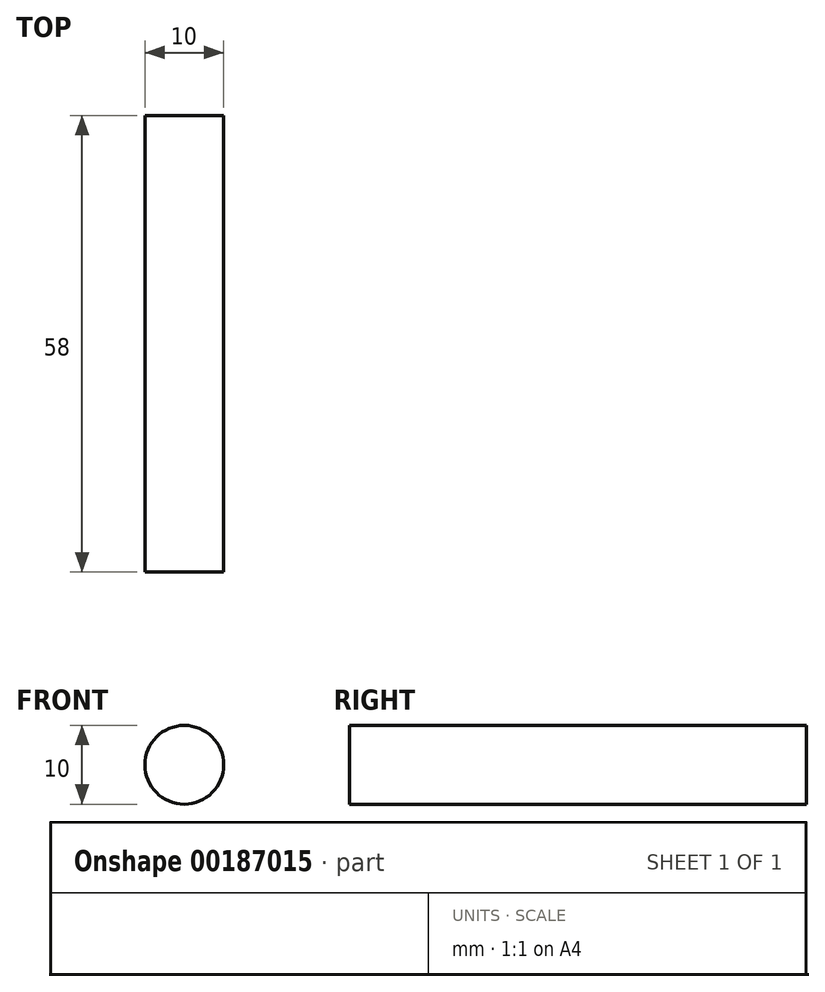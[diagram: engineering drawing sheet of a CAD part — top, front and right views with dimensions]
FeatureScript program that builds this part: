
annotation { "Feature Type Name" : "Feature", "Feature Type Description" : "" }
export const myFeature = defineFeature(function(context is Context, id is Id, definition is map)
    precondition{}
    {
        {
            var Q0;
            Q0=qCreatedBy(makeId("Front.planeOp"),FACE);
            var sketch = newSketch(context, id + "F0", { "sketchPlane" : qUnion([Q0])});
            skCircle(sketch, "E0", {"center": v(0, 0) * mm, "radius": 5 * mm});
            skSolve(sketch);
        }
        {
            var Q0;
            Q0=makeQuery(id+"F0.imprint","IMPRINT",FACE,{"disambiguationData":[TD([[makeQuery(id+"F0.imprint","IMPRINT",EDGE,{"derivedFrom":sQuery(id+"F0.wireOp",EDGE,"E0")}),1.0]])]});
            extrude(context, id + "F1", {"entities" : qUnion([Q0]), "depth" : 58 * mm});
        }
    });
